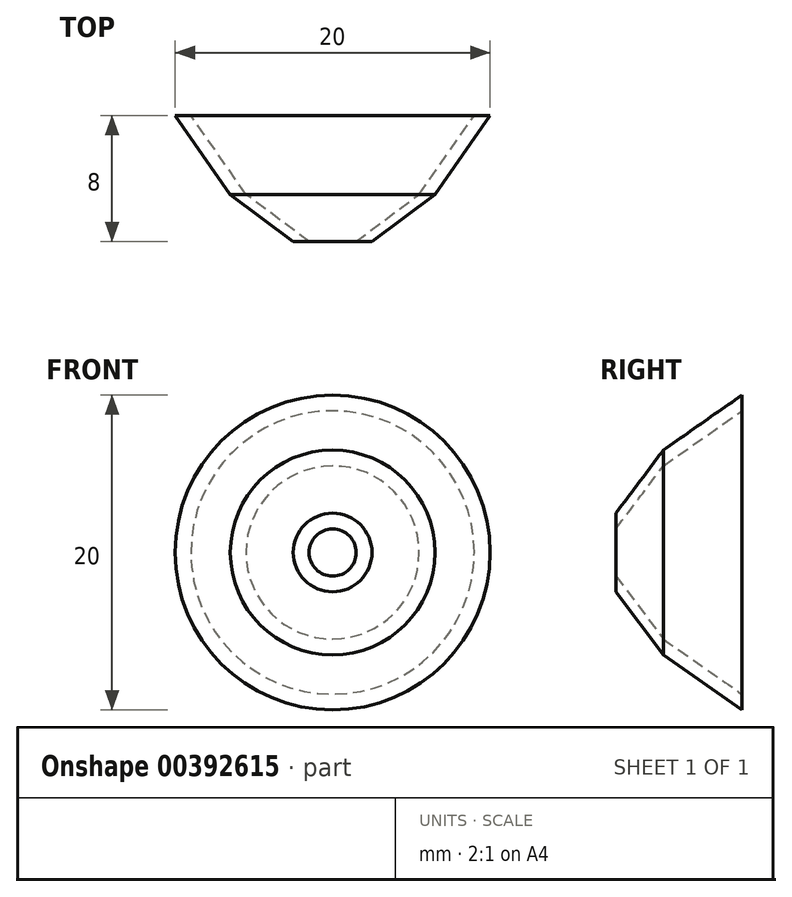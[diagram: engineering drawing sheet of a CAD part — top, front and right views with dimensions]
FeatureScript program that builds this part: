
annotation { "Feature Type Name" : "Feature", "Feature Type Description" : "" }
export const myFeature = defineFeature(function(context is Context, id is Id, definition is map)
    precondition{}
    {
        {
            var Q0;
            Q0=qCreatedBy(makeId("Right.planeOp"),FACE);
            var sketch = newSketch(context, id + "F0", { "sketchPlane" : qUnion([Q0])});
            skLineSegment(sketch, "E0", {"start": v(-3, 9.37) * mm, "end": v(0, 5.37) * mm});
            skLineSegment(sketch, "E1", {"start": v(0, 5.37) * mm, "end": v(0, 6.37) * mm});
            skLineSegment(sketch, "E2", {"start": v(0, 6.37) * mm, "end": v(-3, 10.37) * mm});
            skLineSegment(sketch, "E3", {"start": v(-3, 10.37) * mm, "end": v(-3, 9.37) * mm});
            skLineSegment(sketch, "E4", {"start": v(0, 11.87) * mm, "end": v(-5.54, 11.87) * mm});
            skLineSegment(sketch, "E5", {"start": v(0, 6.37) * mm, "end": v(5, 2.87) * mm});
            skLineSegment(sketch, "E6", {"start": v(0, 5.37) * mm, "end": v(5, 1.87) * mm});
            skLineSegment(sketch, "E7", {"start": v(5, 1.87) * mm, "end": v(5, 2.87) * mm});
            skLineSegment(sketch, "E8", {"start": v(0, 11.87) * mm, "end": v(13.17, 11.87) * mm});
            skSolve(sketch);
        }
        {
            var Q0;
            Q0=makeQuery(id+"F0.imprint","IMPRINT",FACE,{"disambiguationData":[TD([[makeQuery(id+"F0.imprint","IMPRINT",EDGE,{"derivedFrom":sQuery(id+"F0.wireOp",EDGE,"E0")}),1.0]])]});
            var Q1;
            Q1=sQuery(id+"F0.wireOp",EDGE,"E4");
            revolve(context, id + "F1", {"entities" : qUnion([Q0]), "axis" : qUnion([Q1]), "revolveType" : RevolveType.FULL});
        }
        {
            var Q0;
            {var subQ2=sQuery(id+"F0.wireOp",EDGE,"E5");Q0=makeQuery(id+"F0.imprint","IMPRINT",FACE,{"disambiguationData":[TD([[makeQuery(id+"F0.imprint","IMPRINT",EDGE,{"derivedFrom":subQ2}),-1.0]])]});}
            var Q1;
            Q1=sQuery(id+"F0.wireOp",EDGE,"E8");
            revolve(context, id + "F2", {"operationType" : NewBodyOperationType.ADD, "entities" : qUnion([Q0]), "axis" : qUnion([Q1]), "revolveType" : RevolveType.FULL});
        }
    });
